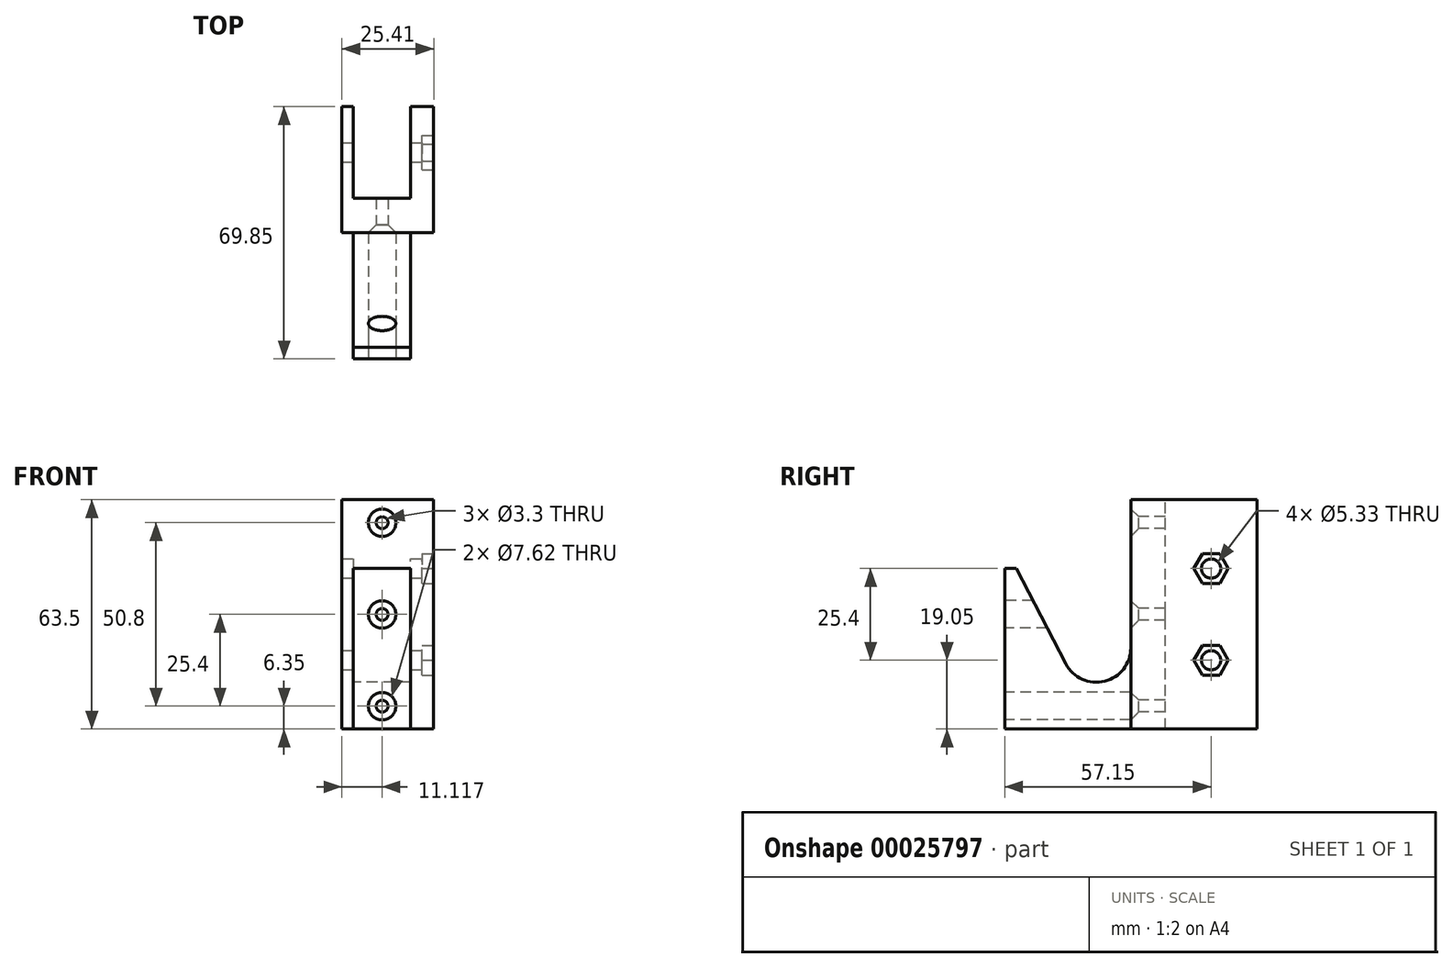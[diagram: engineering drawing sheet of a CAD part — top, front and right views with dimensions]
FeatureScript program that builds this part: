
annotation { "Feature Type Name" : "Feature", "Feature Type Description" : "" }
export const myFeature = defineFeature(function(context is Context, id is Id, definition is map)
    precondition{}
    {
        {
            var Q0;
            Q0=qCreatedBy(makeId("Right.planeOp"),FACE);
            var sketch = newSketch(context, id + "F0", { "sketchPlane" : qUnion([Q0])});
            skLineSegment(sketch, "E0", {"start": v(0, 0) * mm, "end": v(0, 63.5) * mm});
            skLineSegment(sketch, "E1", {"start": v(0, 63.5) * mm, "end": v(-9.53, 63.5) * mm});
            skLineSegment(sketch, "E2", {"start": v(-9.53, 63.5) * mm, "end": v(-9.52, 22.49) * mm});
            skArc(sketch, "E3", {"start": v(-9.52, 22.49) * mm, "mid": v(-16.78, 13.24) * mm, "end": v(-27.5, 18.08) * mm});
            skLineSegment(sketch, "E4", {"start": v(-27.5, 18.08) * mm, "end": v(-41.28, 44.45) * mm});
            skLineSegment(sketch, "E5", {"start": v(-41.28, 44.45) * mm, "end": v(-44.45, 44.45) * mm});
            skLineSegment(sketch, "E6", {"start": v(-44.45, 44.45) * mm, "end": v(-44.45, 0) * mm});
            skLineSegment(sketch, "E7", {"start": v(-44.45, 0) * mm, "end": v(0, 0) * mm});
            skSolve(sketch);
        }
        {
            var Q0;
            Q0=qSketchRegion(id+"F0",true);
            extrude(context, id + "F1", {"entities" : qUnion([Q0]), "depth" : 15.88 * mm});
        }
        {
            var Q0;
            Q0=makeQuery(id+"F1.opExtrude","SWEPT_FACE",FACE,{"disambiguationData":[OSD([sQuery(id+"F0.wireOp",EDGE,"E2")])]});
            var sketch = newSketch(context, id + "F2", { "sketchPlane" : qUnion([Q0])});
            skPoint(sketch, "E8", {"position": v(7.94, 57.15) * mm});
            skPoint(sketch, "E9", {"position": v(7.94, 31.75) * mm});
            skPoint(sketch, "E10", {"position": v(7.94, 6.35) * mm});
            skSolve(sketch);
        }
        {
            var Q0;
            Q0=sQuery(id+"F2.wireOp",VERTEX,"E8");
            var Q1;
            Q1=sQuery(id+"F2.wireOp",VERTEX,"E9");
            var Q2;
            Q2=sQuery(id+"F2.wireOp",VERTEX,"E10");
            var Q3;
            Q3=makeQuery(id+"F1.opExtrude","SWEPT_BODY",BODY,{"disambiguationData":[OSD([sQuery(id+"F0.wireOp",EDGE,"E0"),sQuery(id+"F0.wireOp",EDGE,"E1"),sQuery(id+"F0.wireOp",EDGE,"E2"),sQuery(id+"F0.wireOp",EDGE,"E3"),sQuery(id+"F0.wireOp",EDGE,"E4"),sQuery(id+"F0.wireOp",EDGE,"E5"),sQuery(id+"F0.wireOp",EDGE,"E6"),sQuery(id+"F0.wireOp",EDGE,"E7")])]});
            hole(context, id + "F3", {"style" : HoleStyle.C_SINK, "holeDiameter" : 3.3 * mm, "cSinkDiameter" : 7.62 * mm, "endStyle" : HoleEndStyle.THROUGH, "locations" : qUnion([Q0, Q1, Q2]), "scope" : qUnion([Q3]), "cSinkAngle" : 90 * degree});
        }
        {
            var Q0;
            Q0=makeQuery(id+"F1.opExtrude","SWEPT_FACE",FACE,{"disambiguationData":[OSD([sQuery(id+"F0.wireOp",EDGE,"E6")])]});
            var sketch = newSketch(context, id + "F4", { "sketchPlane" : qUnion([Q0])});
            skCircle(sketch, "E11", {"center": v(7.94, 6.35) * mm, "radius": 3.81 * mm});
            skCircle(sketch, "E12", {"center": v(7.94, 31.75) * mm, "radius": 3.81 * mm});
            skSolve(sketch);
        }
        {
            var Q0;
            Q0=qSketchRegion(id+"F4",true);
            extrude(context, id + "F5", {"entities" : qUnion([Q0]), "operationType" : NewBodyOperationType.REMOVE, "oppositeDirection" : true, "depth" : 34.92 * mm});
        }
        {
            var Q0;
            Q0=makeQuery(id+"F1.opExtrude","CAP_FACE",FACE,{"disambiguationData":[OSD([sQuery(id+"F0.wireOp",EDGE,"E0"),sQuery(id+"F0.wireOp",EDGE,"E1"),sQuery(id+"F0.wireOp",EDGE,"E2"),sQuery(id+"F0.wireOp",EDGE,"E3"),sQuery(id+"F0.wireOp",EDGE,"E4"),sQuery(id+"F0.wireOp",EDGE,"E5"),sQuery(id+"F0.wireOp",EDGE,"E6"),sQuery(id+"F0.wireOp",EDGE,"E7")])],"isStart":true});
            var sketch = newSketch(context, id + "F6", { "sketchPlane" : qUnion([Q0])});
            skLineSegment(sketch, "E13.bottom", {"start": v(9.53, 63.5) * mm, "end": v(-25.4, 63.5) * mm});
            skLineSegment(sketch, "E13.top", {"start": v(9.53, 0) * mm, "end": v(-25.4, 0) * mm});
            skLineSegment(sketch, "E13.left", {"start": v(9.53, 63.5) * mm, "end": v(9.53, 0) * mm});
            skLineSegment(sketch, "E13.right", {"start": v(-25.4, 63.5) * mm, "end": v(-25.4, 0) * mm});
            skSolve(sketch);
        }
        {
            var Q0;
            Q0=qSketchRegion(id+"F6",true);
            extrude(context, id + "F7", {"entities" : qUnion([Q0]), "operationType" : NewBodyOperationType.ADD, "depth" : 3.17 * mm});
        }
        {
            var Q0;
            Q0=makeQuery(id+"F1.opExtrude","CAP_FACE",FACE,{"disambiguationData":[OSD([sQuery(id+"F0.wireOp",EDGE,"E0"),sQuery(id+"F0.wireOp",EDGE,"E1"),sQuery(id+"F0.wireOp",EDGE,"E2"),sQuery(id+"F0.wireOp",EDGE,"E3"),sQuery(id+"F0.wireOp",EDGE,"E4"),sQuery(id+"F0.wireOp",EDGE,"E5"),sQuery(id+"F0.wireOp",EDGE,"E6"),sQuery(id+"F0.wireOp",EDGE,"E7")])],"isStart":false});
            var sketch = newSketch(context, id + "F8", { "sketchPlane" : qUnion([Q0])});
            skLineSegment(sketch, "E14.bottom", {"start": v(-9.53, 63.5) * mm, "end": v(25.4, 63.5) * mm});
            skLineSegment(sketch, "E14.top", {"start": v(-9.53, 0) * mm, "end": v(25.4, 0) * mm});
            skLineSegment(sketch, "E14.left", {"start": v(-9.53, 63.5) * mm, "end": v(-9.53, 0) * mm});
            skLineSegment(sketch, "E14.right", {"start": v(25.4, 63.5) * mm, "end": v(25.4, 0) * mm});
            skSolve(sketch);
        }
        {
            var Q0;
            Q0=qSketchRegion(id+"F8",true);
            extrude(context, id + "F9", {"entities" : qUnion([Q0]), "operationType" : NewBodyOperationType.ADD, "depth" : 6.35 * mm});
        }
        {
            var Q0;
            Q0=makeQuery(id+"F9.opExtrude","CAP_FACE",FACE,{"disambiguationData":[OSD([sQuery(id+"F8.wireOp",EDGE,"E14.bottom"),sQuery(id+"F8.wireOp",EDGE,"E14.top"),sQuery(id+"F8.wireOp",EDGE,"E14.left"),sQuery(id+"F8.wireOp",EDGE,"E14.right")])],"isStart":false});
            var sketch = newSketch(context, id + "F10", { "sketchPlane" : qUnion([Q0])});
            skPoint(sketch, "E15", {"position": v(12.7, 44.45) * mm});
            skPoint(sketch, "E16", {"position": v(12.7, 19.05) * mm});
            skSolve(sketch);
        }
        {
            var Q0;
            Q0=sQuery(id+"F10.wireOp",VERTEX,"E15");
            var Q1;
            Q1=sQuery(id+"F10.wireOp",VERTEX,"E16");
            var Q2;
            Q2=makeQuery(id+"F1.opExtrude","SWEPT_BODY",BODY,{"disambiguationData":[OSD([sQuery(id+"F0.wireOp",EDGE,"E0"),sQuery(id+"F0.wireOp",EDGE,"E1"),sQuery(id+"F0.wireOp",EDGE,"E2"),sQuery(id+"F0.wireOp",EDGE,"E3"),sQuery(id+"F0.wireOp",EDGE,"E4"),sQuery(id+"F0.wireOp",EDGE,"E5"),sQuery(id+"F0.wireOp",EDGE,"E6"),sQuery(id+"F0.wireOp",EDGE,"E7")])]});
            hole(context, id + "F11", {"style" : HoleStyle.SIMPLE, "holeDiameter" : 5.33 * mm, "endStyle" : HoleEndStyle.THROUGH, "locations" : qUnion([Q0, Q1]), "scope" : qUnion([Q2])});
        }
        {
            var Q0;
            Q0=makeQuery(id+"F9.opExtrude","CAP_FACE",FACE,{"disambiguationData":[OSD([sQuery(id+"F8.wireOp",EDGE,"E14.bottom"),sQuery(id+"F8.wireOp",EDGE,"E14.top"),sQuery(id+"F8.wireOp",EDGE,"E14.left"),sQuery(id+"F8.wireOp",EDGE,"E14.right")])],"isStart":false});
            var sketch = newSketch(context, id + "F12", { "sketchPlane" : qUnion([Q0])});
            skCircle(sketch, "E17.cCircle", {"center": v(12.7, 44.45) * mm, "radius": 4.13 * mm, "construction": true});
            skLineSegment(sketch, "E17.0", {"start": v(15.08, 48.58) * mm, "end": v(17.47, 44.45) * mm});
            skLineSegment(sketch, "E17.1", {"start": v(17.47, 44.45) * mm, "end": v(15.08, 40.32) * mm});
            skLineSegment(sketch, "E17.2", {"start": v(15.08, 40.32) * mm, "end": v(10.32, 40.32) * mm});
            skLineSegment(sketch, "E17.3", {"start": v(10.32, 40.32) * mm, "end": v(7.93, 44.45) * mm});
            skLineSegment(sketch, "E17.4", {"start": v(7.93, 44.45) * mm, "end": v(10.32, 48.58) * mm});
            skLineSegment(sketch, "E17.5", {"start": v(10.32, 48.58) * mm, "end": v(15.08, 48.58) * mm});
            skPoint(sketch, "E17.0.midPoint", {"position": v(16.27, 46.51) * mm});
            skCircle(sketch, "E18.cCircle", {"center": v(12.7, 19.05) * mm, "radius": 4.13 * mm, "construction": true});
            skLineSegment(sketch, "E18.0", {"start": v(10.32, 23.18) * mm, "end": v(15.08, 23.18) * mm});
            skLineSegment(sketch, "E18.1", {"start": v(15.08, 23.18) * mm, "end": v(17.47, 19.05) * mm});
            skLineSegment(sketch, "E18.2", {"start": v(17.47, 19.05) * mm, "end": v(15.08, 14.92) * mm});
            skLineSegment(sketch, "E18.3", {"start": v(15.08, 14.92) * mm, "end": v(10.32, 14.92) * mm});
            skLineSegment(sketch, "E18.4", {"start": v(10.32, 14.92) * mm, "end": v(7.93, 19.05) * mm});
            skLineSegment(sketch, "E18.5", {"start": v(7.93, 19.05) * mm, "end": v(10.32, 23.18) * mm});
            skPoint(sketch, "E18.0.midPoint", {"position": v(12.7, 23.18) * mm});
            skSolve(sketch);
        }
        {
            var Q0;
            Q0=qSketchRegion(id+"F12",true);
            extrude(context, id + "F13", {"entities" : qUnion([Q0]), "operationType" : NewBodyOperationType.REMOVE, "oppositeDirection" : true, "depth" : 3.17 * mm});
        }
    });
